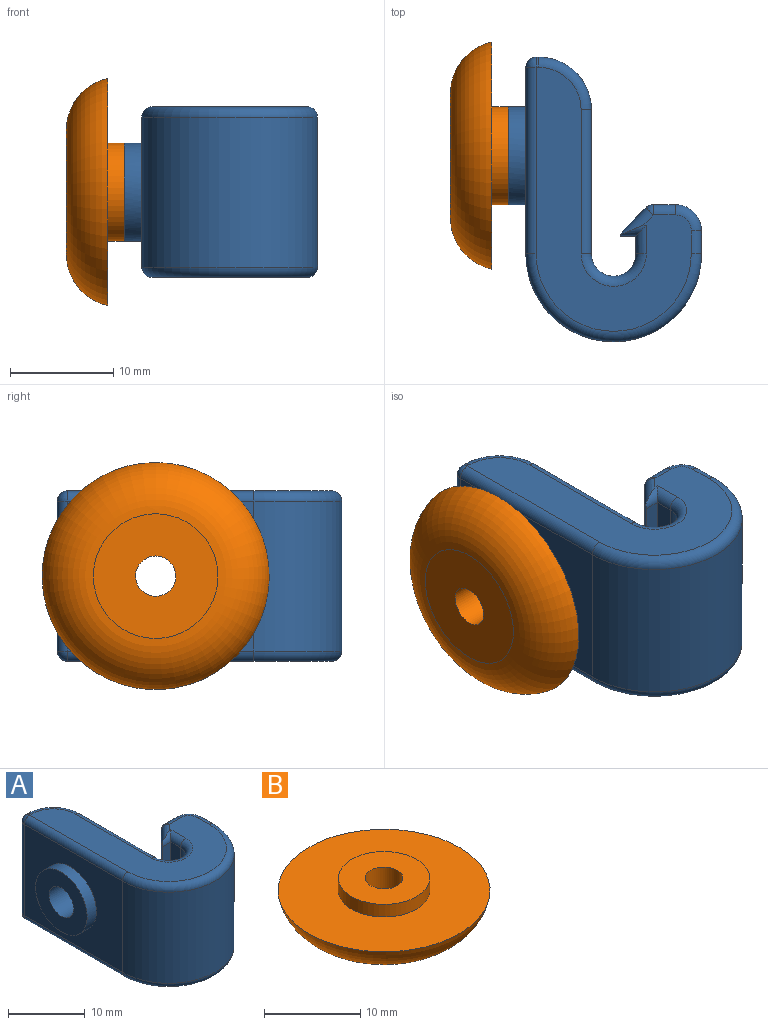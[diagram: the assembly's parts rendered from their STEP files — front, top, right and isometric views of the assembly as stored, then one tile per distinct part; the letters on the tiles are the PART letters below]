
ASSEMBLY  parts=2 mates=1
PART A: 50 faces, bbox 19.4x28.7x16.5 mm
  f0: plane 25.56x15.02mm, normal (0,0,1), area 163.5mm2, adj f21,f25,f26,f31,f36,f38,f39,f41
  f1: plane 25.56x15.02mm, normal (0,0,-1), area 163.5mm2, adj f17,f18,f19,f20,f23,f24,f28,f33
  f2: plane 14.51x1.75mm, normal (-1,0,0), area 25.3mm2, adj f8,f16,f33,f43
  f3: cylinder r=2.25mm len=6.55mm, axis (1,0,0), area 92.6mm2, adj f13,f14
  f4: plane 18.05x14.51mm, normal (-1,0,0), area 191mm2, adj f5,f12,f18,f26,f27
  f5: cylinder r=8.51mm len=17.02mm, axis (0,0,-1), area 387.9mm2, adj f4,f6,f17,f21
  f6: plane 14.51x2.22mm, normal (1,0,0), area 32.2mm2, adj f5,f20,f25,f48
  f7: plane 14.51x2.13mm, normal (0,1,0), area 30.8mm2, adj f24,f30,f31,f48
  f8: cylinder r=2.16mm len=14.51mm, axis (0,0,-1), area 98.4mm2, adj f2,f9,f28,f41
  f9: plane 14.51x13.97mm, normal (1,0,0), area 149.9mm2, adj f8,f15,f23,f39,f45
  f10: plane 14.51x0.27mm, normal (0,1,0), area 3.9mm2, adj f19,f27,f36,f45
  f11: plane 14.51x2.2mm, normal (-0.71,0.71,0), area 45.2mm2, adj f30,f34,f38,f40
  f12: cylinder r=4.75mm len=9.5mm, axis (1,0,0), area 50.7mm2, adj f4,f13
  f13: plane 9.5x9.5mm, normal (-1,0,0), area 55mm2, adj f3,f12
  f14: plane 8.2x8.2mm, normal (1,0,0), area 36.9mm2, adj f3,f15
  f15: cylinder r=4.1mm len=8.2mm, axis (1,0,0), area 38.6mm2, adj f9,f14
  f16: plane 14.51x1.5mm, normal (0,-1,0), area 21.8mm2, adj f2,f37,f40,f42
  f17: torus R=7.51mm, axis (0,0,1), area 40.2mm2, adj f1,f5,f18,f20
  f18: cylinder r=1mm len=18.05mm, axis (0,-1,0), area 28.4mm2, adj f1,f4,f17,f22
  f19: cylinder r=1mm len=1mm, axis (-1,0,0), area 0.4mm2, adj f1,f10,f22,f46
  f20: cylinder r=1mm len=2.22mm, axis (0,1,0), area 3.5mm2, adj f1,f6,f17,f49
  f21: torus R=7.51mm, axis (0,0,1), area 40.2mm2, adj f0,f5,f25,f26
  f22: sphere r=1mm, area 1.6mm2, adj f18,f19,f27
  f23: cylinder r=1mm len=13.97mm, axis (0,1,0), area 21.9mm2, adj f1,f9,f28,f46
  f24: cylinder r=1mm len=2.13mm, axis (-1,0,0), area 3.3mm2, adj f1,f7,f29,f49
  f25: cylinder r=1mm len=2.22mm, axis (0,-1,0), area 3.5mm2, adj f0,f6,f21,f47
  f26: cylinder r=1mm len=18.05mm, axis (0,1,0), area 28.4mm2, adj f0,f4,f21,f32
  f27: cylinder r=1mm len=14.51mm, axis (0,0,1), area 22.8mm2, adj f4,f10,f22,f32
  f28: torus R=3.16mm, axis (0,0,1), area 12.4mm2, adj f1,f8,f23,f33
  f29: sphere r=1mm, area 0.8mm2, adj f24,f30,f34
  f30: cylinder r=1mm len=14.51mm, axis (0,0,-1), area 11.4mm2, adj f7,f11,f29,f35
  f31: cylinder r=1mm len=2.13mm, axis (1,0,0), area 3.3mm2, adj f0,f7,f35,f47
  f32: sphere r=1mm, area 1.6mm2, adj f26,f27,f36
  f33: cylinder r=1mm len=2.75mm, axis (0,-1,0), area 3.3mm2, adj f1,f2,f28,f37
  f34: cylinder r=1mm len=3.24mm, axis (0.71,0.71,0), area 4.5mm2, adj f1,f11,f29,f37,f40
  f35: sphere r=1mm, area 0.8mm2, adj f30,f31,f38
  f36: cylinder r=1mm len=1mm, axis (1,0,0), area 0.4mm2, adj f0,f10,f32,f44
  f37: cylinder r=1mm len=2.5mm, axis (-1,0,0), area 1.9mm2, adj f1,f16,f33,f34,f40
  f38: cylinder r=1mm len=3.24mm, axis (0.71,0.71,0), area 4.5mm2, adj f0,f11,f35,f40,f42
  f39: cylinder r=1mm len=13.97mm, axis (0,-1,0), area 21.9mm2, adj f0,f9,f41,f44
  f40: cylinder r=1mm len=15.44mm, axis (0,0,1), area 9mm2, adj f11,f16,f34,f37,f38,f42
  f41: torus R=3.16mm, axis (0,0,1), area 12.4mm2, adj f0,f8,f39,f43
  f42: cylinder r=1mm len=2.5mm, axis (1,0,0), area 1.9mm2, adj f0,f16,f38,f40,f43
  f43: cylinder r=1mm len=2.75mm, axis (0,1,0), area 3.3mm2, adj f0,f2,f41,f42
  f44: torus R=4.08mm, axis (0,0,1), area 11.6mm2, adj f0,f36,f39,f45
  f45: cylinder r=5.08mm len=14.51mm, axis (0,0,-1), area 115.8mm2, adj f9,f10,f44,f46
  f46: torus R=4.08mm, axis (0,0,1), area 11.6mm2, adj f1,f19,f23,f45
  f47: torus R=1.54mm, axis (0,0,1), area 5.4mm2, adj f0,f25,f31,f48
  f48: cylinder r=2.54mm len=14.51mm, axis (0,0,-1), area 57.9mm2, adj f6,f7,f47,f49
  f49: torus R=1.54mm, axis (0,0,1), area 5.4mm2, adj f1,f20,f24,f48
PART B: 6 faces, bbox 24.1x24.1x5.6 mm
  f0: plane 22x22mm, normal (0,0,1), area 309.3mm2, adj f3,f5
  f1: plane 12.07x12.07mm, normal (0,0,-1), area 102.5mm2, adj f2,f5
  f2: cylinder r=1.95mm len=5.6mm, axis (0,0,-1), area 68.6mm2, adj f1,f4
  f3: cylinder r=4.75mm len=9.5mm, axis (0,0,-1), area 47.8mm2, adj f0,f4
  f4: plane 9.5x9.5mm, normal (0,0,1), area 58.9mm2, adj f2,f3
  f5: torus R=6.04mm, axis (0,0,-1), area 389mm2, adj f0,f1
PLACE A t=(-8.07,6.43,-3.26)mm
PLACE B rot(axis=(0.71,0,0.71),180deg) t=(-18.55,6.43,5)mm
MATE fastened B.f3 <-> A.f12  axis (1,0,0) through (-12.95,6.43,5)mm
